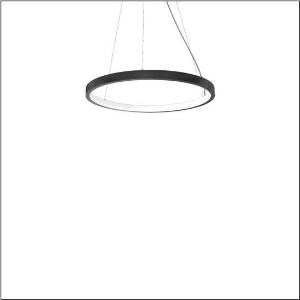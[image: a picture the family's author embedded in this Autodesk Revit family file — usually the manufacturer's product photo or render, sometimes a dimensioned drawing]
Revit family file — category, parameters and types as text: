
# Revit family: silica_r__21_ring-i_5pjbi2d3104a_3dac
name_source: partatom
category: Lighting Fixtures
units: mm (PartAtom-declared; Revit-internal decimal feet)

## family parameters
Cut with Voids When Loaded = No
Host = Face
Light Source = No
Part Type = Normal
Room Calculation Point = No
Round Connector Dimension = Use Diameter
Shared = No

## types (1)
- Silica® 21 Ring-I (1 x LED, 5040 lm, 80 W, 4000K)
    Apparent Load = 80 VA
    CIE Flux Codes = 22 48 76 50 101
    Color Rendering = 80
    Color Temperature = 4000K
    Default Elevation = 1800 mm
    Description = Silica® 21 Ring-I, suspended luminaire, of PMMA, frosted, light emission: inner ring side luminous distribution, primary light characteristic: symmetric, installation type: suspended mounting, LED, rated luminous flux: 5.040lm, luminous efficacy: 63lm/W, light colour: 840, colour temperature: 4000K, with terminal, 5-pole, mains connection: 230V, AC/DC, 0/50..60Hz, rated input power: 80W, housing, of extruded aluminium section, jet black (RAL 9005), diameter: 805mm, ceiling canopy, jet black (RAL 9005), protection rating (lamp compartment): IP40, insulation class (complete): insulation class I (protective earthing), certification: CE, impact resistance: IK02, permissible operating ambient temperature: 0..+35°C, packaging unit: 1 piece
    Height = 48 mm  [stored 0.15748 ft]
    Lamp = 1 x LED
    Lamp Light Flux = 5040 lm
    Lamp Power = 80 W
    Lamp count = 1
    Length = 805 mm
    Luminous efficacy = 63 lm/W
    Manufacturer = Siteco
    ModVariant = No
    Model = 5PJBI2D3104A
    Mounting Place = Ceiling
    Mounting Type = Pendant
    Number of Poles = 1
    OnlyDefault = Yes
    Power Factor = 1
    Product Name = Silica® 21 Ring-I
    Product group = suspended luminaire
    ProductGroupID = 904
    Protection Class = Protection class I
    Protection Degree = IP 40
    RLX_Detail_Level = 1
    RLX_Emergency_Light_Flux = 0 lm
    RLX_Emergency_Type = 0
    RLX_Emergency_Type_DB = No
    RlxData = <blob elided: 13917 chars, md5=ce3647b5>
    Socket = socket
    Standby Power = 0 W
    System Light Flux = 5040 lm
    System Power = 80 W
    Type Comments = Product without accessories
    Type Image = l_1258365.jpg
    URL = http://relux.com
    VarID = ---
    Voltage = 0 V
    Weight = 0.00 kg
    Width = 0 mm  [stored 0 ft]

note: [stored X ft] marks values corroborated as IEEE doubles in the binary element streams (Revit-internal decimal feet)

## geometry (parser evidence)
native form markers: Sweep x12
no freeform markers — native parametric forms only
